# Revit family: Filter-Effluent-Clarus-170-0078
name_source: partatom
category: Pipe Accessories
revit_build: Autodesk Revit 2014 (Build: 20130308_1515(x64)
units: mm (PartAtom-declared; Revit-internal decimal feet)

## types (1)
- 170-0078
    170-0144 4" Sanitary Tee = Yes
    Assembly Code = D2010900
    Default Elevation = 0"
    Description = Residential Effluent Filters
    Discharge Diameter = 4" Sanitary Outlet
    Discharge Radius = 2"
    Filter Area = 132 Linear Feet
    Filtration Size = 1/16"
    Flow Rate = 1,500 gpd (5.7 m³/day)
    Height = 24 7/32"
    Installation Type = Floor Mounted
    Manufacturer = Clarus
    Material = Polypropylene-Clarus-Blue
    Model = 170-0078
    Price = Prices may vary. Please consult Manufacturer Representative for most up-to-date price list.
    Product Documentation Link = https://www.clarusenvironmental.com
    Product Page URL = https://www.clarusenvironmental.com
    URL = https://www.clarusenvironmental.com
    Warranty Information = Lifetime Warranty
    Waste Connection = Yes
    Width = 4 1/8"

## geometry (parser evidence)
native form markers: Sweep x1
no freeform markers — native parametric forms only
